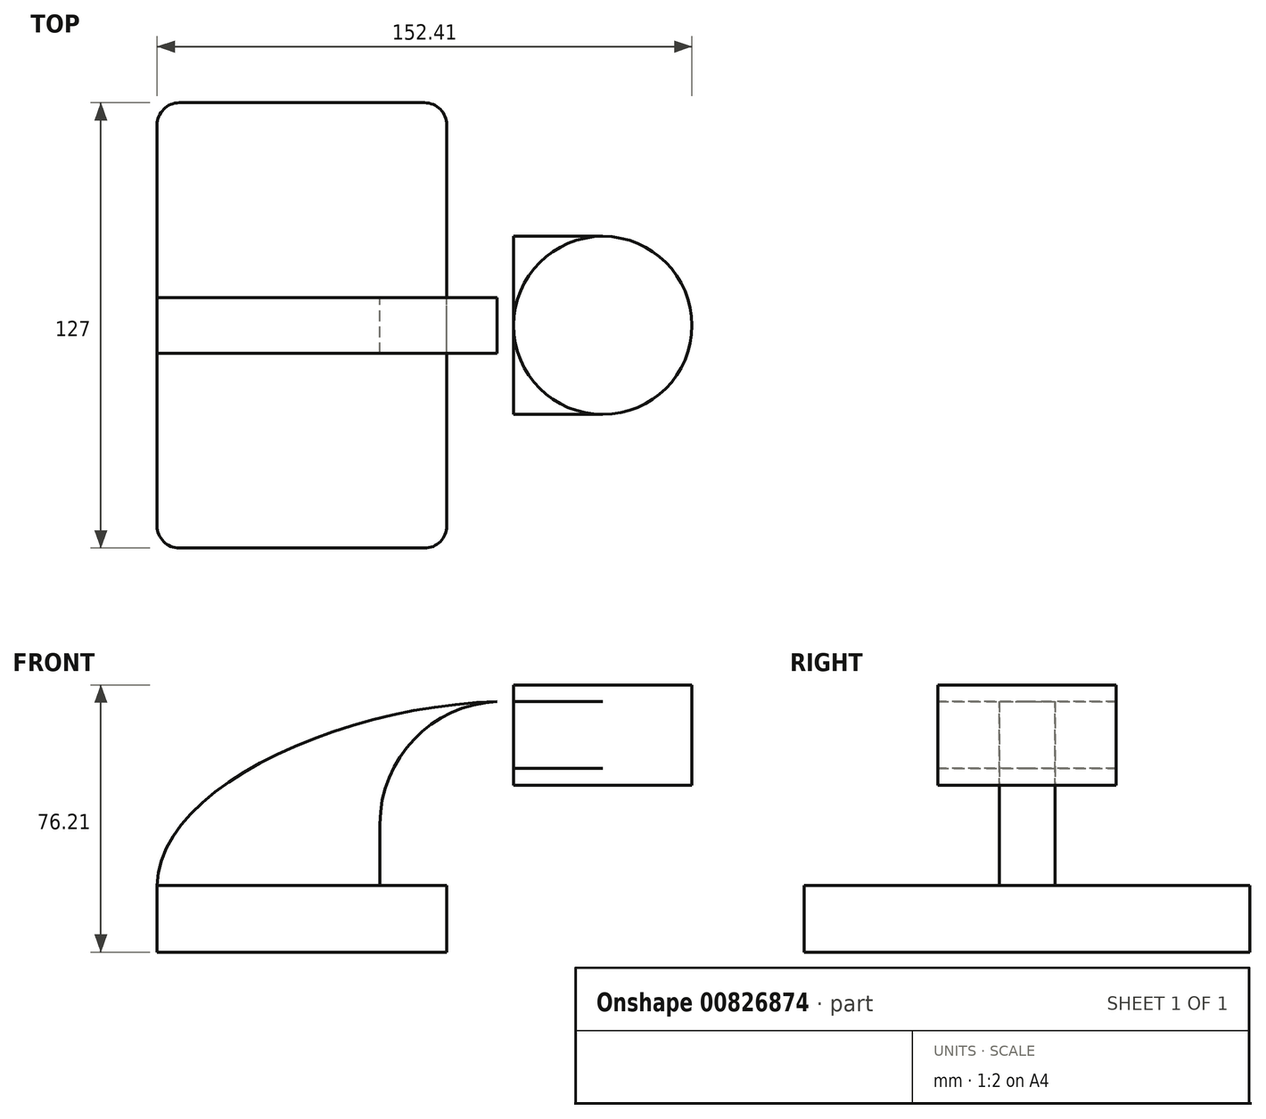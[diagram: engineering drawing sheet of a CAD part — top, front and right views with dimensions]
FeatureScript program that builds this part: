
annotation { "Feature Type Name" : "Feature", "Feature Type Description" : "" }
export const myFeature = defineFeature(function(context is Context, id is Id, definition is map)
    precondition{}
    {
        {
            var Q0;
            Q0=qCreatedBy(makeId("Front.planeOp"),FACE);
            var sketch = newSketch(context, id + "F0", { "sketchPlane" : qUnion([Q0])});
            skLineSegment(sketch, "E0.bottom", {"start": v(41.28, 9.53) * mm, "end": v(-41.28, 9.53) * mm});
            skLineSegment(sketch, "E0.top", {"start": v(41.28, -9.53) * mm, "end": v(-41.28, -9.53) * mm});
            skLineSegment(sketch, "E0.left", {"start": v(41.28, 9.53) * mm, "end": v(41.28, -9.53) * mm});
            skLineSegment(sketch, "E0.right", {"start": v(-41.28, 9.53) * mm, "end": v(-41.28, -9.53) * mm});
            skPoint(sketch, "E0.middle", {"position": v(0, 0) * mm});
            skLineSegment(sketch, "E1.bottom", {"start": v(111.12, 66.67) * mm, "end": v(60.33, 66.67) * mm});
            skLineSegment(sketch, "E1.top", {"start": v(111.13, 38.1) * mm, "end": v(60.33, 38.1) * mm});
            skLineSegment(sketch, "E1.left", {"start": v(111.12, 66.68) * mm, "end": v(111.13, 38.1) * mm});
            skLineSegment(sketch, "E1.right", {"start": v(60.33, 66.68) * mm, "end": v(60.33, 38.1) * mm});
            skPoint(sketch, "E1.middle", {"position": v(85.73, 52.39) * mm});
            skArc(sketch, "E2", {"start": v(41.28, 27) * mm, "mid": v(45.92, 38.23) * mm, "end": v(57.15, 42.88) * mm});
            skLineSegment(sketch, "E3", {"start": v(57.15, 42.88) * mm, "end": v(85.73, 42.88) * mm});
            skLineSegment(sketch, "E4", {"start": v(41.28, 9.53) * mm, "end": v(41.28, 27) * mm});
            skLineSegment(sketch, "E5.0", {"start": v(57.15, 61.93) * mm, "end": v(85.73, 61.93) * mm});
            skArc(sketch, "E5.1", {"start": v(22.23, 27) * mm, "mid": v(32.45, 51.7) * mm, "end": v(57.15, 61.93) * mm});
            skLineSegment(sketch, "E5.2", {"start": v(22.23, 9.53) * mm, "end": v(22.23, 27) * mm});
            skFitSpline(sketch, "E6", {"points": [v(-41.28, 9.53) * mm, v(57.15, 61.93) * mm], "startDerivative": vector(0.84, 83.77) * mm, "endDerivative": vector(136.06, 2.21) * mm});
            skLineSegment(sketch, "E7", {"start": v(85.73, 38.1) * mm, "end": v(85.73, 66.67) * mm});
            skSolve(sketch);
        }
        {
            var Q0;
            Q0=makeQuery(id+"F0.imprint","IMPRINT",FACE,{"disambiguationData":[TD([[makeQuery(id+"F0.imprint","IMPRINT",EDGE,{"derivedFrom":sQuery(id+"F0.wireOp",EDGE,"E0.top")}),-1.0]])]});
            extrude(context, id + "F1", {"entities" : qUnion([Q0]), "endBound" : BoundingType.SYMMETRIC, "depth" : 127 * mm, "offsetDistance" : 25.4 * mm});
        }
        {
            var Q0;
            {var subQ1=sQuery(id+"F0.wireOp",EDGE,"E2");Q0=makeQuery(id+"F0.imprint","IMPRINT",FACE,{"disambiguationData":[TD([[makeQuery(id+"F0.imprint","IMPRINT",EDGE,{"derivedFrom":subQ1}),1.0]])]});}
            var Q1;
            {var subQ0=sQuery(id+"F0.wireOp",EDGE,"E5.0");var subQ1=sQuery(id+"F0.wireOp",EDGE,"E1.right");var subQ2=makeQuery(id+"F0.imprint","INTERSECT",VERTEX,{"derivedFrom":[subQ1,subQ0]});Q1=makeQuery(id+"F0.imprint","IMPRINT",FACE,{"disambiguationData":[TD([[makeQuery(id+"F0.imprint","IMPRINT",EDGE,{"disambiguationData":[TD([[subQ2,-1.0]])],"derivedFrom":subQ1}),1.0]])]});}
            extrude(context, id + "F2", {"entities" : qUnion([Q0, Q1]), "operationType" : NewBodyOperationType.ADD, "endBound" : BoundingType.SYMMETRIC, "depth" : 50.8 * mm, "offsetDistance" : 25.4 * mm});
        }
        {
            var Q0;
            {var subQ3=sQuery(id+"F0.wireOp",EDGE,"E5.2");Q0=makeQuery(id+"F0.imprint","IMPRINT",FACE,{"disambiguationData":[TD([[makeQuery(id+"F0.imprint","IMPRINT",EDGE,{"derivedFrom":subQ3}),1.0]])]});}
            extrude(context, id + "F3", {"entities" : qUnion([Q0]), "operationType" : NewBodyOperationType.ADD, "endBound" : BoundingType.SYMMETRIC, "depth" : 15.88 * mm, "offsetDistance" : 25.4 * mm});
        }
        {
            var Q0;
            {var subQ4=sQuery(id+"F0.wireOp",EDGE,"E1.left");Q0=makeQuery(id+"F0.imprint","IMPRINT",FACE,{"disambiguationData":[TD([[makeQuery(id+"F0.imprint","IMPRINT",EDGE,{"derivedFrom":subQ4}),-1.0]])]});}
            var Q1;
            Q1=sQuery(id+"F0.wireOp",EDGE,"E7");
            revolve(context, id + "F4", {"operationType" : NewBodyOperationType.ADD, "surfaceOperationType" : NewSurfaceOperationType.NEW, "entities" : qUnion([Q0]), "axis" : qUnion([Q1]), "revolveType" : RevolveType.FULL});
        }
        {
            var Q0;
            Q0=makeQuery(id+"F1.opExtrude","CAP_EDGE",EDGE,{"disambiguationData":[OSD([sQuery(id+"F0.wireOp",EDGE,"E0.left")])],"isStart":false});
            var Q1;
            Q1=makeQuery(id+"F1.opExtrude","CAP_EDGE",EDGE,{"disambiguationData":[OSD([sQuery(id+"F0.wireOp",EDGE,"E0.right")])],"isStart":false});
            var Q2;
            Q2=makeQuery(id+"F1.opExtrude","CAP_EDGE",EDGE,{"disambiguationData":[OSD([sQuery(id+"F0.wireOp",EDGE,"E0.left")])],"isStart":true});
            var Q3;
            Q3=makeQuery(id+"F1.opExtrude","CAP_EDGE",EDGE,{"disambiguationData":[OSD([sQuery(id+"F0.wireOp",EDGE,"E0.right")])],"isStart":true});
            fillet(context, id + "F5", {"entities" : qUnion([Q0, Q1, Q2, Q3]), "radius" : 6.35 * mm, "tangentPropagation" : true, "allowEdgeOverflow" : false});
        }
    });
